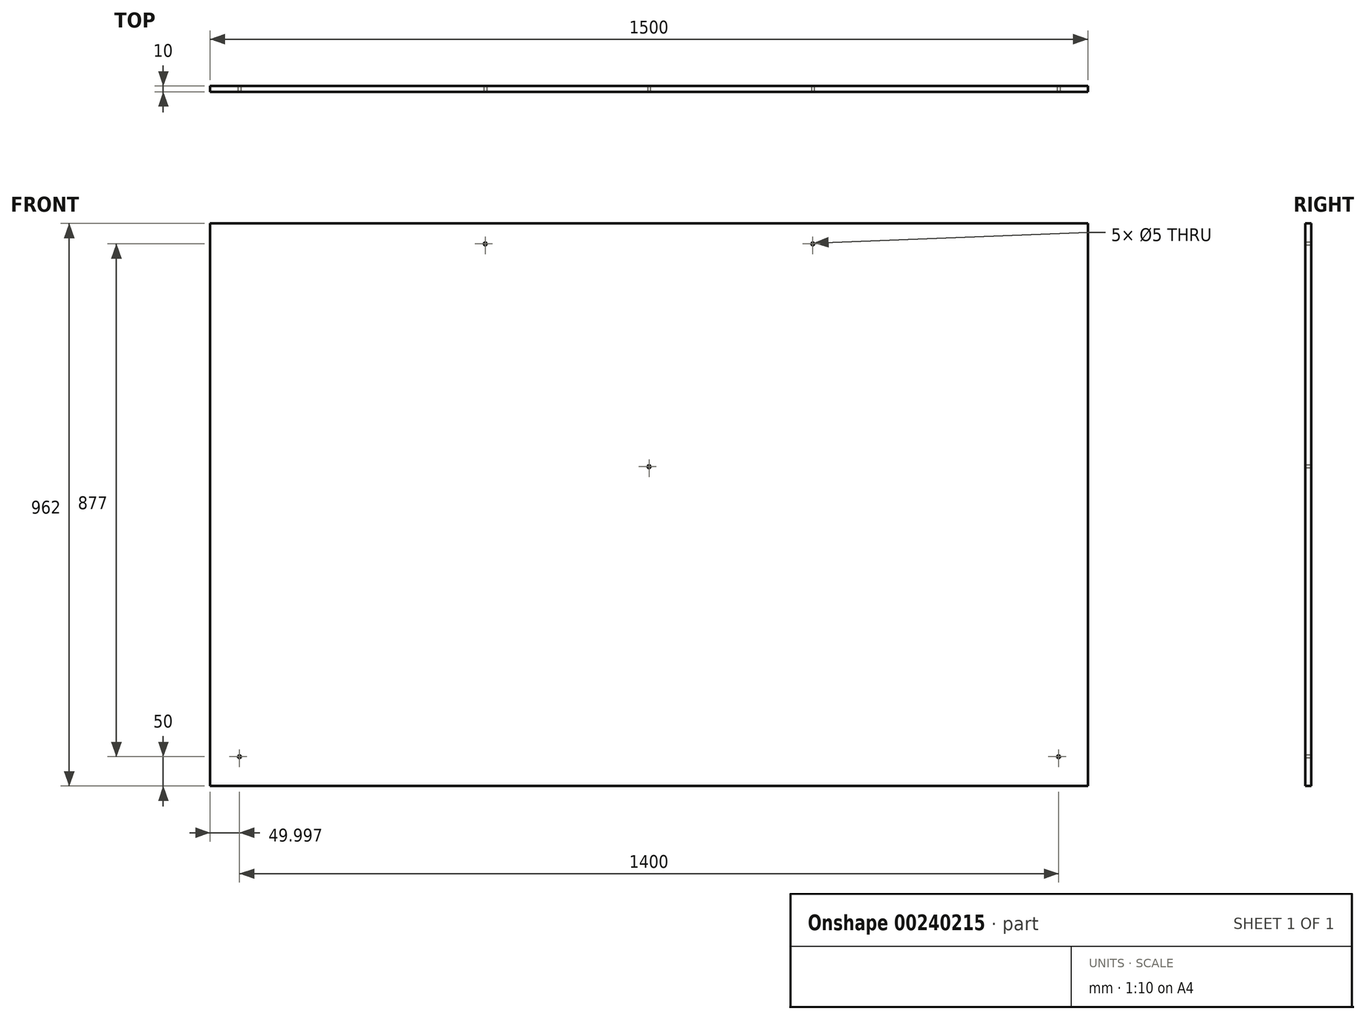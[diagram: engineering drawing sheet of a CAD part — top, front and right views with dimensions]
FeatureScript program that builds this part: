
annotation { "Feature Type Name" : "Feature", "Feature Type Description" : "" }
export const myFeature = defineFeature(function(context is Context, id is Id, definition is map)
    precondition{}
    {
        {
            var Q0;
            Q0=qCreatedBy(makeId("Front.planeOp"),FACE);
            var sketch = newSketch(context, id + "F0", { "sketchPlane" : qUnion([Q0])});
            skLineSegment(sketch, "E0.bottom", {"start": v(-753.24, 445.77) * mm, "end": v(746.76, 445.77) * mm});
            skLineSegment(sketch, "E0.top", {"start": v(-753.24, -516.23) * mm, "end": v(746.76, -516.23) * mm});
            skLineSegment(sketch, "E0.left", {"start": v(-753.24, 445.77) * mm, "end": v(-753.24, -516.23) * mm});
            skLineSegment(sketch, "E0.right", {"start": v(746.76, 445.77) * mm, "end": v(746.76, -516.23) * mm});
            skSolve(sketch);
        }
        {
            var Q0;
            Q0=makeQuery(id+"F0.imprint","IMPRINT",FACE,{"disambiguationData":[TD([[makeQuery(id+"F0.imprint","IMPRINT",EDGE,{"derivedFrom":sQuery(id+"F0.wireOp",EDGE,"E0.bottom")}),-1.0]])]});
            extrude(context, id + "F1", {"entities" : qUnion([Q0]), "depth" : 10 * mm});
        }
        {
            var Q0;
            Q0=makeQuery(id+"F1.opExtrude","CAP_FACE",FACE,{"disambiguationData":[OSD([sQuery(id+"F0.wireOp",EDGE,"E0.bottom"),sQuery(id+"F0.wireOp",EDGE,"E0.top"),sQuery(id+"F0.wireOp",EDGE,"E0.left"),sQuery(id+"F0.wireOp",EDGE,"E0.right")])],"isStart":false});
            var sketch = newSketch(context, id + "F2", { "sketchPlane" : qUnion([Q0])});
            skCircle(sketch, "E1", {"center": v(-703.24, -466.23) * mm, "radius": 2.5 * mm});
            skCircle(sketch, "E2", {"center": v(696.76, -466.23) * mm, "radius": 2.5 * mm});
            skLineSegment(sketch, "E3", {"start": v(-753.24, -466.23) * mm, "end": v(-703.24, -466.23) * mm, "construction": true});
            skLineSegment(sketch, "E4", {"start": v(696.76, -466.23) * mm, "end": v(746.76, -466.23) * mm, "construction": true});
            skLineSegment(sketch, "E5", {"start": v(696.76, -466.23) * mm, "end": v(-703.24, -466.23) * mm, "construction": true});
            skSolve(sketch);
        }
        {
            var Q0;
            Q0 = qSketchRegion(id + "F2", true);
            extrude(context, id + "F3", {"entities" : qUnion([Q0]), "operationType" : NewBodyOperationType.REMOVE, "endBound" : BoundingType.THROUGH_ALL, "oppositeDirection" : true, "depth" : 25 * mm});
        }
        {
            var Q0;
            Q0=makeQuery(id+"F1.opExtrude","CAP_FACE",FACE,{"disambiguationData":[OSD([sQuery(id+"F0.wireOp",EDGE,"E0.bottom"),sQuery(id+"F0.wireOp",EDGE,"E0.top"),sQuery(id+"F0.wireOp",EDGE,"E0.left"),sQuery(id+"F0.wireOp",EDGE,"E0.right")])],"isStart":false});
            var sketch = newSketch(context, id + "F4", { "sketchPlane" : qUnion([Q0])});
            skLineSegment(sketch, "E6", {"start": v(-753.24, 410.77) * mm, "end": v(-283.24, 410.77) * mm, "construction": true});
            skLineSegment(sketch, "E7", {"start": v(-283.24, 410.77) * mm, "end": v(276.76, 410.77) * mm, "construction": true});
            skLineSegment(sketch, "E8", {"start": v(276.76, 410.77) * mm, "end": v(746.76, 410.77) * mm, "construction": true});
            skCircle(sketch, "E9", {"center": v(-283.24, 410.77) * mm, "radius": 2.5 * mm});
            skCircle(sketch, "E10", {"center": v(276.76, 410.77) * mm, "radius": 2.5 * mm});
            skSolve(sketch);
        }
        {
            var Q0;
            Q0 = qSketchRegion(id + "F4", true);
            extrude(context, id + "F5", {"entities" : qUnion([Q0]), "operationType" : NewBodyOperationType.REMOVE, "endBound" : BoundingType.THROUGH_ALL, "oppositeDirection" : true, "depth" : 25 * mm});
        }
        {
            var Q0;
            Q0=makeQuery(id+"F1.opExtrude","CAP_FACE",FACE,{"disambiguationData":[OSD([sQuery(id+"F0.wireOp",EDGE,"E0.bottom"),sQuery(id+"F0.wireOp",EDGE,"E0.top"),sQuery(id+"F0.wireOp",EDGE,"E0.left"),sQuery(id+"F0.wireOp",EDGE,"E0.right")])],"isStart":false});
            var sketch = newSketch(context, id + "F6", { "sketchPlane" : qUnion([Q0])});
            skLineSegment(sketch, "E11", {"start": v(-753.24, 29.77) * mm, "end": v(-3.24, 29.77) * mm, "construction": true});
            skLineSegment(sketch, "E12", {"start": v(-3.24, 29.77) * mm, "end": v(746.76, 29.77) * mm, "construction": true});
            skLineSegment(sketch, "E13", {"start": v(-3.24, 29.77) * mm, "end": v(-3.24, 445.77) * mm, "construction": true});
            skCircle(sketch, "E14", {"center": v(-3.24, 29.77) * mm, "radius": 2.5 * mm});
            skSolve(sketch);
        }
        {
            var Q0;
            Q0 = qSketchRegion(id + "F6", true);
            extrude(context, id + "F7", {"entities" : qUnion([Q0]), "operationType" : NewBodyOperationType.REMOVE, "endBound" : BoundingType.THROUGH_ALL, "oppositeDirection" : true, "depth" : 25 * mm});
        }
    });
